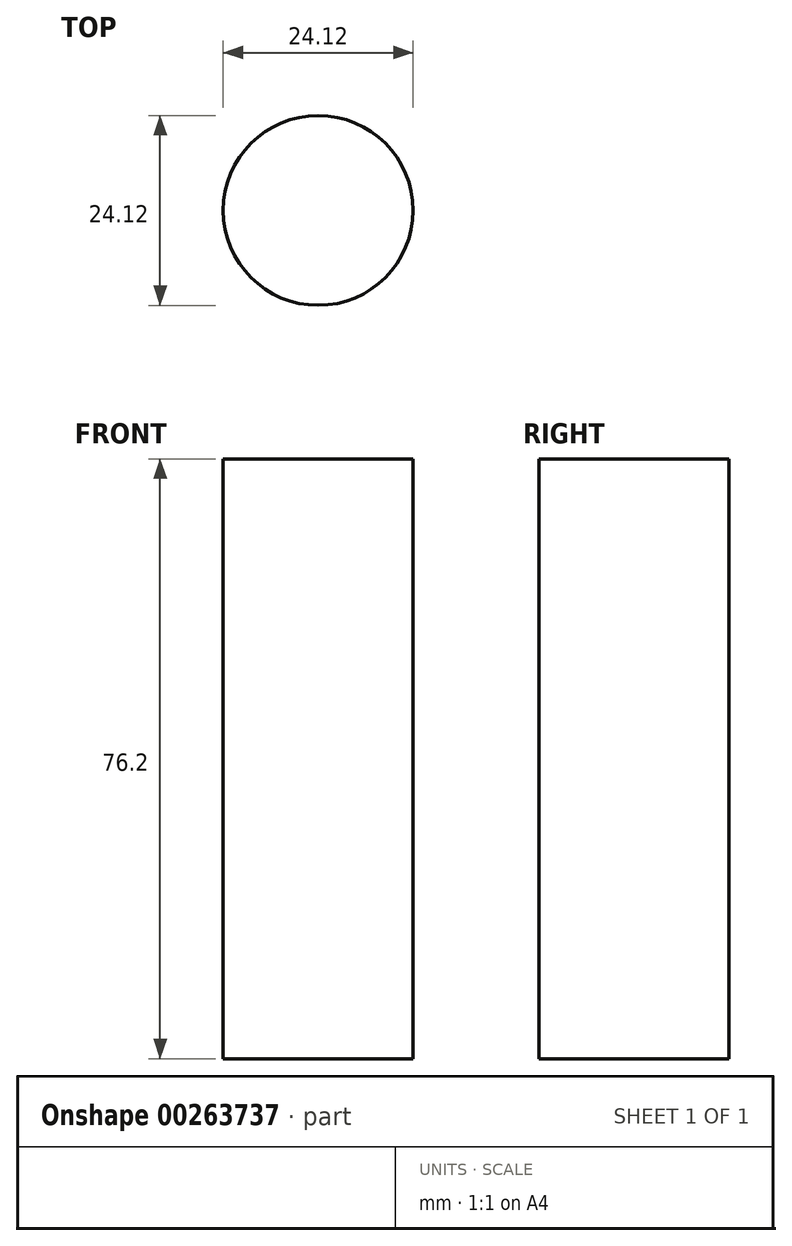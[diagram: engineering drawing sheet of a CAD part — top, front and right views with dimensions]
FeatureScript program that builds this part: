
annotation { "Feature Type Name" : "Feature", "Feature Type Description" : "" }
export const myFeature = defineFeature(function(context is Context, id is Id, definition is map)
    precondition{}
    {
        {
            var Q0;
            Q0=qCreatedBy(makeId("Top.planeOp"),FACE);
            var sketch = newSketch(context, id + "F0", { "sketchPlane" : qUnion([Q0])});
            skCircle(sketch, "E0", {"center": v(0, 0) * mm, "radius": 12.06 * mm});
            skSolve(sketch);
        }
        {
            var Q0;
            Q0 = qSketchRegion(id + "F0", true);
            extrude(context, id + "F1", {"entities" : qUnion([Q0]), "depth" : 101.6 * mm});
        }
        {
            var Q0;
            Q0=makeQuery(id+"F1.opExtrude","SWEPT_BODY",BODY,{"disambiguationData":[OSD([sQuery(id+"F0.wireOp",EDGE,"E0")])]});
            deleteBodies(context, id + "F2", {"entities" : qUnion([Q0])});
        }
        {
            var Q0;
            Q0 = qSketchRegion(id + "F0", true);
            extrude(context, id + "F3", {"entities" : qUnion([Q0]), "depth" : 76.2 * mm});
        }
    });
